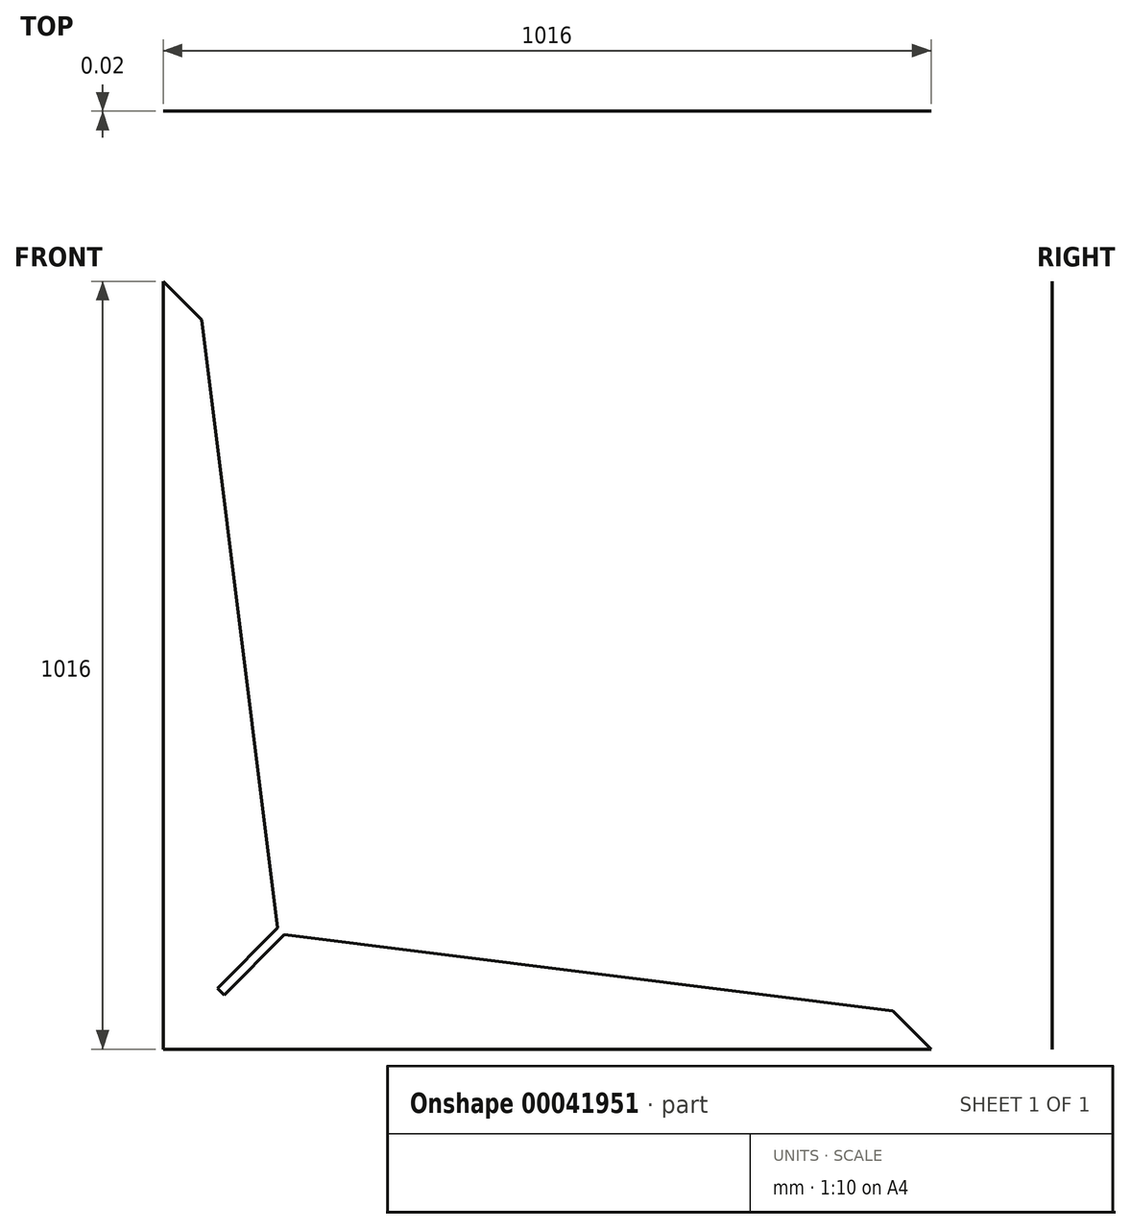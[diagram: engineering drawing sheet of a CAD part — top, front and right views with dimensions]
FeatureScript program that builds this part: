
annotation { "Feature Type Name" : "Feature", "Feature Type Description" : "" }
export const myFeature = defineFeature(function(context is Context, id is Id, definition is map)
    precondition{}
    {
        {
            var Q0;
            Q0=qCreatedBy(makeId("Front.planeOp"),FACE);
            var sketch = newSketch(context, id + "F0", { "sketchPlane" : qUnion([Q0])});
            skLineSegment(sketch, "E0", {"start": v(-364.07, 651.93) * mm, "end": v(-364.07, -364.07) * mm});
            skLineSegment(sketch, "E1", {"start": v(-364.07, -364.07) * mm, "end": v(651.93, -364.07) * mm});
            skLineSegment(sketch, "E2", {"start": v(-364.07, 651.93) * mm, "end": v(-313.27, 601.13) * mm});
            skLineSegment(sketch, "E3", {"start": v(-313.27, 601.13) * mm, "end": v(-211.67, -211.67) * mm});
            skLineSegment(sketch, "E4", {"start": v(-211.67, -211.67) * mm, "end": v(601.13, -313.27) * mm});
            skLineSegment(sketch, "E5", {"start": v(651.93, -364.07) * mm, "end": v(601.13, -313.27) * mm});
            skSolve(sketch);
        }
        {
            var Q0;
            Q0=makeQuery(id+"F0.imprint","IMPRINT",FACE,{"disambiguationData":[TD([[makeQuery(id+"F0.imprint","IMPRINT",EDGE,{"derivedFrom":sQuery(id+"F0.wireOp",EDGE,"E0")}),1.0]])]});
            var Q1;
            Q1=sQuery(id+"F0.wireOp",EDGE,"E0");
            var Q2;
            Q2=sQuery(id+"F0.wireOp",EDGE,"E1");
            var Q3;
            Q3=sQuery(id+"F0.wireOp",EDGE,"E2");
            var Q4;
            Q4=sQuery(id+"F0.wireOp",EDGE,"E3");
            var Q5;
            Q5=sQuery(id+"F0.wireOp",EDGE,"E4");
            var Q6;
            Q6=sQuery(id+"F0.wireOp",EDGE,"E5");
            extrude(context, id + "F1", {"entities" : qUnion([Q0]), "surfaceEntities" : qUnion([Q1, Q2, Q3, Q4, Q5, Q6]), "depth" : 1 / 50.8 * mm});
        }
        {
            var Q0;
            Q0=makeQuery(id+"F1.opExtrude","CAP_FACE",FACE,{"disambiguationData":[OSD([sQuery(id+"F0.wireOp",EDGE,"E0"),sQuery(id+"F0.wireOp",EDGE,"E1"),sQuery(id+"F0.wireOp",EDGE,"E2"),sQuery(id+"F0.wireOp",EDGE,"E3"),sQuery(id+"F0.wireOp",EDGE,"E4"),sQuery(id+"F0.wireOp",EDGE,"E5")])],"isStart":false});
            var sketch = newSketch(context, id + "F2", { "sketchPlane" : qUnion([Q0])});
            skLineSegment(sketch, "E6", {"start": v(-287.87, -287.87) * mm, "end": v(-283.38, -292.36) * mm});
            skLineSegment(sketch, "E7.MirrorCS", {"start": v(-287.87, -287.87) * mm, "end": v(-292.36, -283.38) * mm});
            skLineSegment(sketch, "E8", {"start": v(-292.36, -283.38) * mm, "end": v(-212.66, -203.68) * mm});
            skLineSegment(sketch, "E9", {"start": v(-283.38, -292.36) * mm, "end": v(-203.68, -212.66) * mm});
            skLineSegment(sketch, "E10", {"start": v(-203.68, -212.66) * mm, "end": v(-212.66, -203.68) * mm});
            skSolve(sketch);
        }
        {
            var Q0;
            Q0 = qSketchRegion(id + "F2", true);
            extrude(context, id + "F3", {"entities" : qUnion([Q0]), "operationType" : NewBodyOperationType.REMOVE, "oppositeDirection" : true, "depth" : 25.4 * mm});
        }
    });
